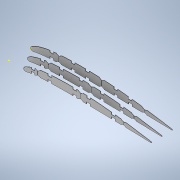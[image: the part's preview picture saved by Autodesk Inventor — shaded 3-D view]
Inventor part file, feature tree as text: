
AUTODESK INVENTOR PART (.ipt)
format: ipt  version: 2022 (Build 260153000, 153)  size: 1,031,168 bytes
history: native  units: mm
features: sketch x21, loft x4, plane x2, extrude x1
ambient origin geometry x8: Origin, YZ Plane, XZ Plane, XY Plane, X Axis, Y Axis, Z Axis, Center Point
bodies: Body1 (feature_tree)
feature tree (28):
  sketch  "Sketch3"  dims[d29=150.0mm d35=2.0mm]
  sketch  "Sketch4"  dims[d36=90.0deg d37=2.0mm]
  sketch  "Sketch5"  dims[d38=90.0deg d43=2.0mm]
  sketch  "Sketch6"  dims[d44=2.0mm d51=2.0mm]
  plane  "Work Plane2"
  sketch  "Sketch9"  dims[d52=2.0mm d56=2.0mm]
  sketch  "Sketch10"  dims[d57=2.0mm]
  sketch  "Sketch14"  dims[d65=2.0mm]
  sketch  "Sketch15"  dims[d66=2.0mm]
  sketch  "Sketch16"  dims[d69=2.0mm]
  sketch  "Sketch17"  dims[d70=2.0mm]
  sketch  "Sketch18"  dims[d76=2.0mm]
  sketch  "Sketch28"  dims[d77=0.0mm]
  sketch  "Sketch29"  dims[d150=1.8mm]
  sketch  "Sketch30"  dims[d151=1.8mm]
  sketch  "Sketch31"  dims[d156=1.8mm]
  sketch  "Sketch32"  dims[d157=1.8mm]
  sketch  "Sketch33"  dims[d167=1.8mm]
  sketch  "Sketch34"  dims[d168=90.0deg]
  sketch  "Sketch35"  dims[d169=1.8mm]
  loft  "Loft3"
  loft  "Loft4"
  loft  "Loft5"
  loft  "Loft6"
  plane  "Work Plane3"
  extrude  "Extrusion3"  Depth=2.0mm
  sketch  "Sketch37"  dims[d175=1.8mm d176=1.8mm d187=1.8mm d188=1.8mm d193=1.8mm d194=90.0deg d195=1.8mm d196=90.0deg d203=25.0mm d204=25.0mm d205=25.0mm d206=25.0mm d207=25.0mm d208=25.0mm d209=25.0mm d210=25.0mm d211=25.0mm d212=25.0mm d213=25.0mm d214=25.0mm d215=25.0mm d216=25.0mm d217=25.0mm d218=25.0mm d219=25.0mm d220=25.0mm d221=25.0mm d222=25.0mm d223=25.0mm d224=25.0mm d225=25.0mm d226=25.0mm d227=25.0mm d228=25.0mm d229=25.0mm d230=25.0mm d231=25.0mm d232=25.0mm d233=25.0mm d234=25.0mm d235=25.0mm d236=25.0mm d237=25.0mm d238=25.0mm d239=25.0mm d240=25.0mm d241=25.0mm d242=25.0mm d249=2.0mm d250=2.0mm d251=2.0mm d252=2.0mm d253=2.0mm d254=2.0mm d255=2.0mm d256=2.0mm d257=2.0mm d258=2.0mm d259=2.0mm d260=2.0mm d261=2.0mm d262=2.0mm d263=2.0mm d264=2.0mm d265=2.0mm d266=2.0mm d267=2.0mm d268=2.0mm d269=2.0mm d270=2.0mm d271=2.0mm d272=2.0mm d277=0.0mm d278=90.0deg d279=0.0mm d280=90.0deg d281=0.0mm d282=90.0deg d283=0.0mm d284=90.0deg d285=0.0mm d286=90.0deg d287=0.0mm d288=90.0deg d289=0.0mm d290=90.0deg d291=0.0mm d292=90.0deg d293=300.0mm d295=5000.0mm d296=2.0mm d297=5000.0mm d298=72.0mm d299=5000.0mm d300=2.0mm d301=5000.0mm d302=72.0mm d303=5000.0mm d304=0.0mm d6=0.5mm d7=0.872665mm d8=0.5mm d9=0.872665mm]
  sketch  "Sketch36"  dims[d170=90.0deg]
